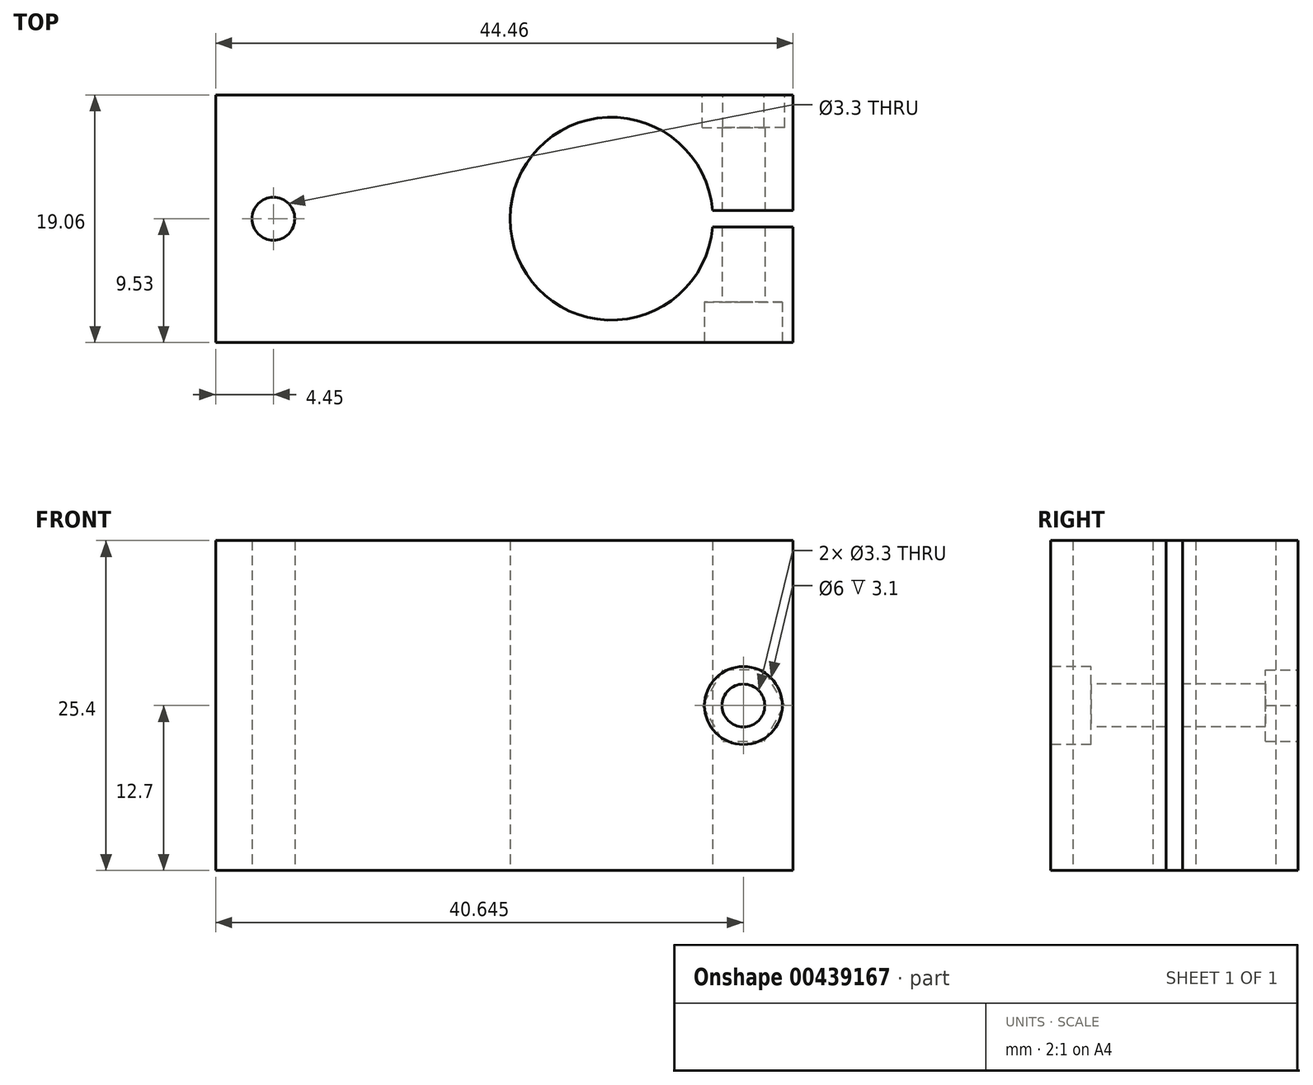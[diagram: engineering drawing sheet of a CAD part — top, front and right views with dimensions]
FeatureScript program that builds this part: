
annotation { "Feature Type Name" : "Feature", "Feature Type Description" : "" }
export const myFeature = defineFeature(function(context is Context, id is Id, definition is map)
    precondition{}
    {
        {
            var Q0;
            Q0=qCreatedBy(makeId("Top.planeOp"),FACE);
            var sketch = newSketch(context, id + "F0", { "sketchPlane" : qUnion([Q0])});
            skLineSegment(sketch, "E0.bottom", {"start": v(-22.22, 9.53) * mm, "end": v(22.22, 9.52) * mm});
            skLineSegment(sketch, "E0.top", {"start": v(-22.22, -9.52) * mm, "end": v(22.22, -9.53) * mm});
            skLineSegment(sketch, "E0.left", {"start": v(-22.22, 9.53) * mm, "end": v(-22.23, -9.53) * mm});
            skLineSegment(sketch, "E0.right", {"start": v(22.22, 9.53) * mm, "end": v(22.22, -9.53) * mm});
            skCircle(sketch, "E1", {"center": v(8.26, 0) * mm, "radius": 7.81 * mm});
            skLineSegment(sketch, "E2.bottom", {"start": v(8.26, 0.64) * mm, "end": v(22.22, 0.64) * mm});
            skLineSegment(sketch, "E2.top", {"start": v(8.26, -0.64) * mm, "end": v(22.22, -0.64) * mm});
            skLineSegment(sketch, "E2.left", {"start": v(8.26, 0.64) * mm, "end": v(8.26, -0.64) * mm});
            skLineSegment(sketch, "E2.right", {"start": v(22.22, 0.64) * mm, "end": v(22.22, -0.64) * mm});
            skCircle(sketch, "E3", {"center": v(-17.78, 0) * mm, "radius": 1.65 * mm});
            skSolve(sketch);
        }
        {
            var Q0;
            {var subQ1=sQuery(id+"F0.wireOp",EDGE,"E0.bottom");Q0=makeQuery(id+"F0.imprint","IMPRINT",FACE,{"disambiguationData":[TD([[makeQuery(id+"F0.imprint","IMPRINT",EDGE,{"derivedFrom":subQ1}),-1.0]])]});}
            extrude(context, id + "F1", {"entities" : qUnion([Q0]), "endBound" : BoundingType.SYMMETRIC, "depth" : 25.4 * mm});
        }
        {
            var Q0;
            Q0=qCreatedBy(makeId("Front.planeOp"),FACE);
            var sketch = newSketch(context, id + "F2", { "sketchPlane" : qUnion([Q0])});
            skCircle(sketch, "E4", {"center": v(-8.9, 0) * mm, "radius": 6.48 * mm});
            skLineSegment(sketch, "E5.0.0", {"start": v(-22.23, -12.7) * mm, "end": v(22.22, -12.7) * mm, "construction": true});
            skLineSegment(sketch, "E5.0.1", {"start": v(22.22, -12.7) * mm, "end": v(22.22, 12.7) * mm, "construction": true});
            skLineSegment(sketch, "E5.0.2", {"start": v(22.22, 12.7) * mm, "end": v(-22.23, 12.7) * mm, "construction": true});
            skLineSegment(sketch, "E5.0.3", {"start": v(-22.23, 12.7) * mm, "end": v(-22.23, -12.7) * mm, "construction": true});
            skLineSegment(sketch, "E6.bottom", {"start": v(-8.9, 0.63) * mm, "end": v(-22.23, 0.63) * mm});
            skLineSegment(sketch, "E6.top", {"start": v(-8.9, -0.63) * mm, "end": v(-22.23, -0.63) * mm});
            skLineSegment(sketch, "E6.left", {"start": v(-8.9, 0.63) * mm, "end": v(-8.9, -0.63) * mm});
            skLineSegment(sketch, "E6.right", {"start": v(-22.23, 0.64) * mm, "end": v(-22.23, -0.64) * mm});
            skCircle(sketch, "E7", {"center": v(18.41, 0) * mm, "radius": 1.65 * mm});
            skSolve(sketch);
        }
        {
            var Q0;
            Q0=makeQuery(id+"F2.imprint","IMPRINT",FACE,{"disambiguationData":[TD([[makeQuery(id+"F2.imprint","IMPRINT",EDGE,{"derivedFrom":sQuery(id+"F2.wireOp",EDGE,"E7")}),1.0]])]});
            extrude(context, id + "F3", {"entities" : qUnion([Q0]), "operationType" : NewBodyOperationType.REMOVE, "endBound" : BoundingType.SYMMETRIC, "oppositeDirection" : true, "depth" : 50.8 * mm});
        }
        {
            var Q0;
            Q0=makeQuery(id+"F1.opExtrude","SWEPT_FACE",FACE,{"disambiguationData":[OSD([sQuery(id+"F0.wireOp",EDGE,"E0.top")])]});
            var sketch = newSketch(context, id + "F4", { "sketchPlane" : qUnion([Q0])});
            skCircle(sketch, "E8", {"center": v(18.41, 0) * mm, "radius": 3 * mm});
            skSolve(sketch);
        }
        {
            var Q0;
            Q0=makeQuery(id+"F4.imprint","IMPRINT",FACE,{"disambiguationData":[TD([[makeQuery(id+"F4.imprint","IMPRINT",EDGE,{"derivedFrom":sQuery(id+"F4.wireOp",EDGE,"E8")}),1.0]])]});
            extrude(context, id + "F5", {"entities" : qUnion([Q0]), "operationType" : NewBodyOperationType.REMOVE, "oppositeDirection" : true, "depth" : 3.1 * mm});
        }
        {
            var Q0;
            Q0=makeQuery(id+"F1.opExtrude","SWEPT_FACE",FACE,{"disambiguationData":[OSD([sQuery(id+"F0.wireOp",EDGE,"E0.bottom")])]});
            var sketch = newSketch(context, id + "F6", { "sketchPlane" : qUnion([Q0])});
            skCircle(sketch, "E9.cCircle", {"center": v(-18.41, 0) * mm, "radius": 2.75 * mm, "construction": true});
            skLineSegment(sketch, "E9.0", {"start": v(-20, 2.75) * mm, "end": v(-16.83, 2.75) * mm});
            skLineSegment(sketch, "E9.1", {"start": v(-16.83, 2.75) * mm, "end": v(-15.24, 0) * mm});
            skLineSegment(sketch, "E9.2", {"start": v(-15.24, 0) * mm, "end": v(-16.83, -2.75) * mm});
            skLineSegment(sketch, "E9.3", {"start": v(-16.83, -2.75) * mm, "end": v(-20, -2.75) * mm});
            skLineSegment(sketch, "E9.4", {"start": v(-20, -2.75) * mm, "end": v(-21.6, 0) * mm});
            skLineSegment(sketch, "E9.5", {"start": v(-21.6, 0) * mm, "end": v(-20, 2.75) * mm});
            skPoint(sketch, "E9.0.midPoint", {"position": v(-18.41, 2.75) * mm});
            skSolve(sketch);
        }
        {
            var Q0;
            Q0=makeQuery(id+"F6.imprint","IMPRINT",FACE,{"disambiguationData":[TD([[makeQuery(id+"F6.imprint","IMPRINT",EDGE,{"derivedFrom":sQuery(id+"F6.wireOp",EDGE,"E9.0")}),-1.0]])]});
            extrude(context, id + "F7", {"entities" : qUnion([Q0]), "operationType" : NewBodyOperationType.REMOVE, "oppositeDirection" : true, "depth" : 2.5 * mm});
        }
    });
